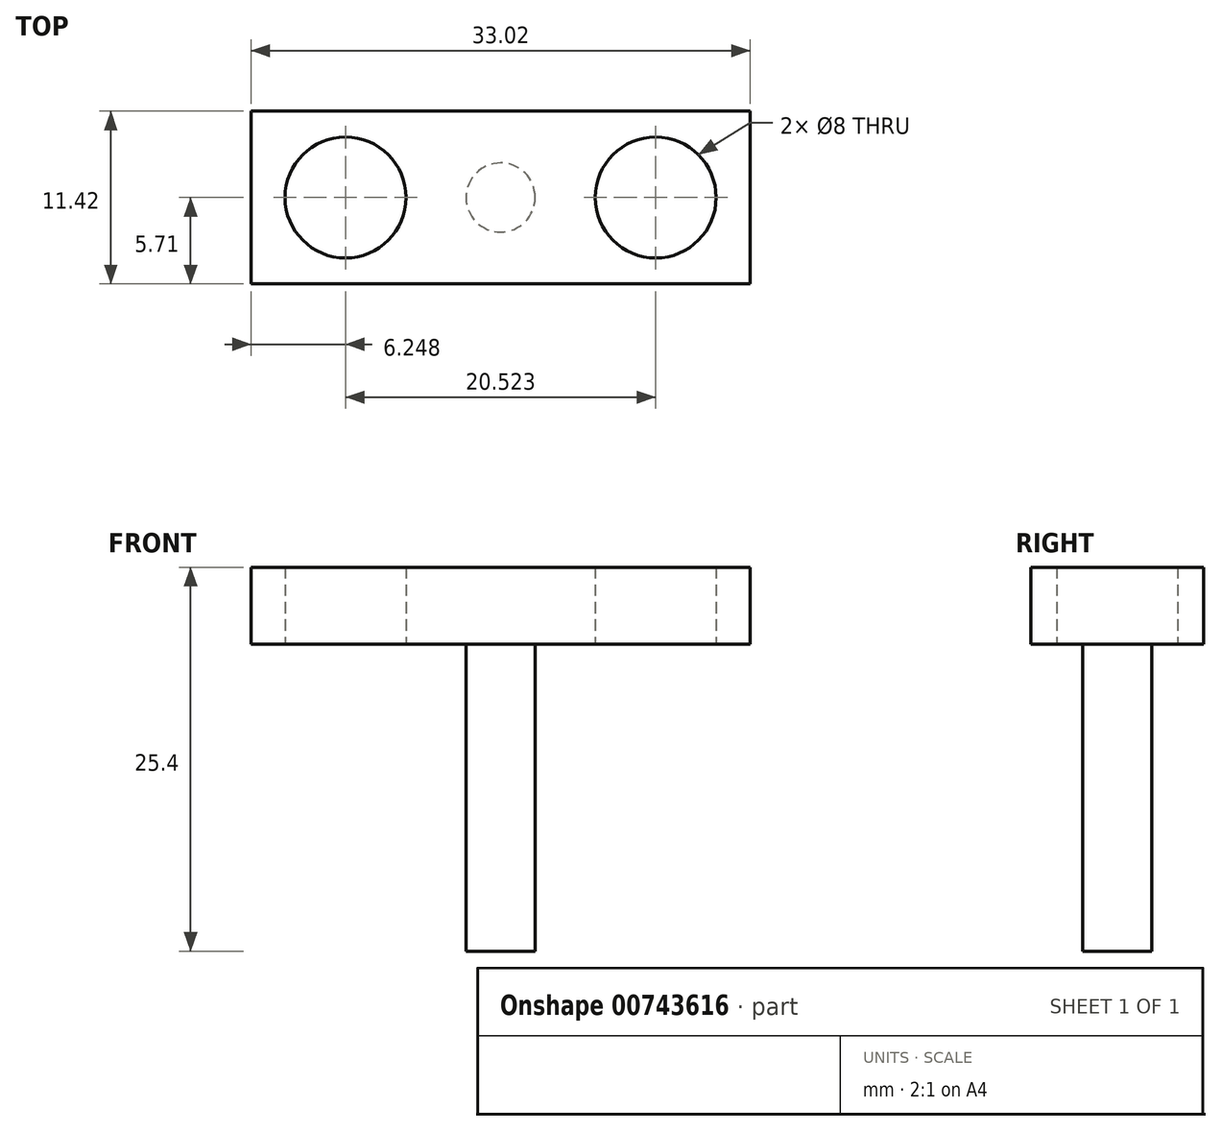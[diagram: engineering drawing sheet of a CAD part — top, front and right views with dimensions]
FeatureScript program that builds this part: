
annotation { "Feature Type Name" : "Feature", "Feature Type Description" : "" }
export const myFeature = defineFeature(function(context is Context, id is Id, definition is map)
    precondition{}
    {
        {
            var Q0;
            Q0=qCreatedBy(makeId("Top.planeOp"),FACE);
            var sketch = newSketch(context, id + "F0", { "sketchPlane" : qUnion([Q0])});
            skLineSegment(sketch, "E0.bottom", {"start": v(-16.51, 5.71) * mm, "end": v(16.51, 5.71) * mm});
            skLineSegment(sketch, "E0.top", {"start": v(-16.51, -5.72) * mm, "end": v(16.51, -5.72) * mm});
            skLineSegment(sketch, "E0.left", {"start": v(-16.51, 5.71) * mm, "end": v(-16.51, -5.72) * mm});
            skLineSegment(sketch, "E0.right", {"start": v(16.51, 5.71) * mm, "end": v(16.51, -5.72) * mm});
            skPoint(sketch, "E0.middle", {"position": v(0, 0) * mm});
            skCircle(sketch, "E1", {"center": v(-10.26, 0) * mm, "radius": 4 * mm});
            skCircle(sketch, "E2", {"center": v(0, 0) * mm, "radius": 3.98 * mm, "construction": true});
            skCircle(sketch, "E3.MirrorC", {"center": v(10.26, 0) * mm, "radius": 4 * mm});
            skSolve(sketch);
        }
        {
            var Q0;
            Q0=makeQuery(id+"F0.imprint","IMPRINT",FACE,{"disambiguationData":[TD([[makeQuery(id+"F0.imprint","IMPRINT",EDGE,{"derivedFrom":sQuery(id+"F0.wireOp",EDGE,"E0.bottom")}),-1.0]])]});
            extrude(context, id + "F1", {"entities" : qUnion([Q0]), "depth" : 5.08 * mm, "offsetDistance" : 25.4 * mm});
        }
        {
            var Q0;
            Q0=makeQuery(id+"F1.opExtrude","CAP_FACE",FACE,{"disambiguationData":[OSD([sQuery(id+"F0.wireOp",EDGE,"E0.bottom"),sQuery(id+"F0.wireOp",EDGE,"E0.top"),sQuery(id+"F0.wireOp",EDGE,"E0.left"),sQuery(id+"F0.wireOp",EDGE,"E0.right"),sQuery(id+"F0.wireOp",EDGE,"E1"),sQuery(id+"F0.wireOp",EDGE,"E3.MirrorC")])],"isStart":true});
            var sketch = newSketch(context, id + "F2", { "sketchPlane" : qUnion([Q0])});
            skCircle(sketch, "E4", {"center": v(0, 0) * mm, "radius": 2.29 * mm});
            skSolve(sketch);
        }
        {
            var Q0;
            Q0 = qSketchRegion(id + "F2", true);
            extrude(context, id + "F3", {"entities" : qUnion([Q0]), "operationType" : NewBodyOperationType.ADD, "depth" : 20.32 * mm, "offsetDistance" : 25.4 * mm});
        }
    });
